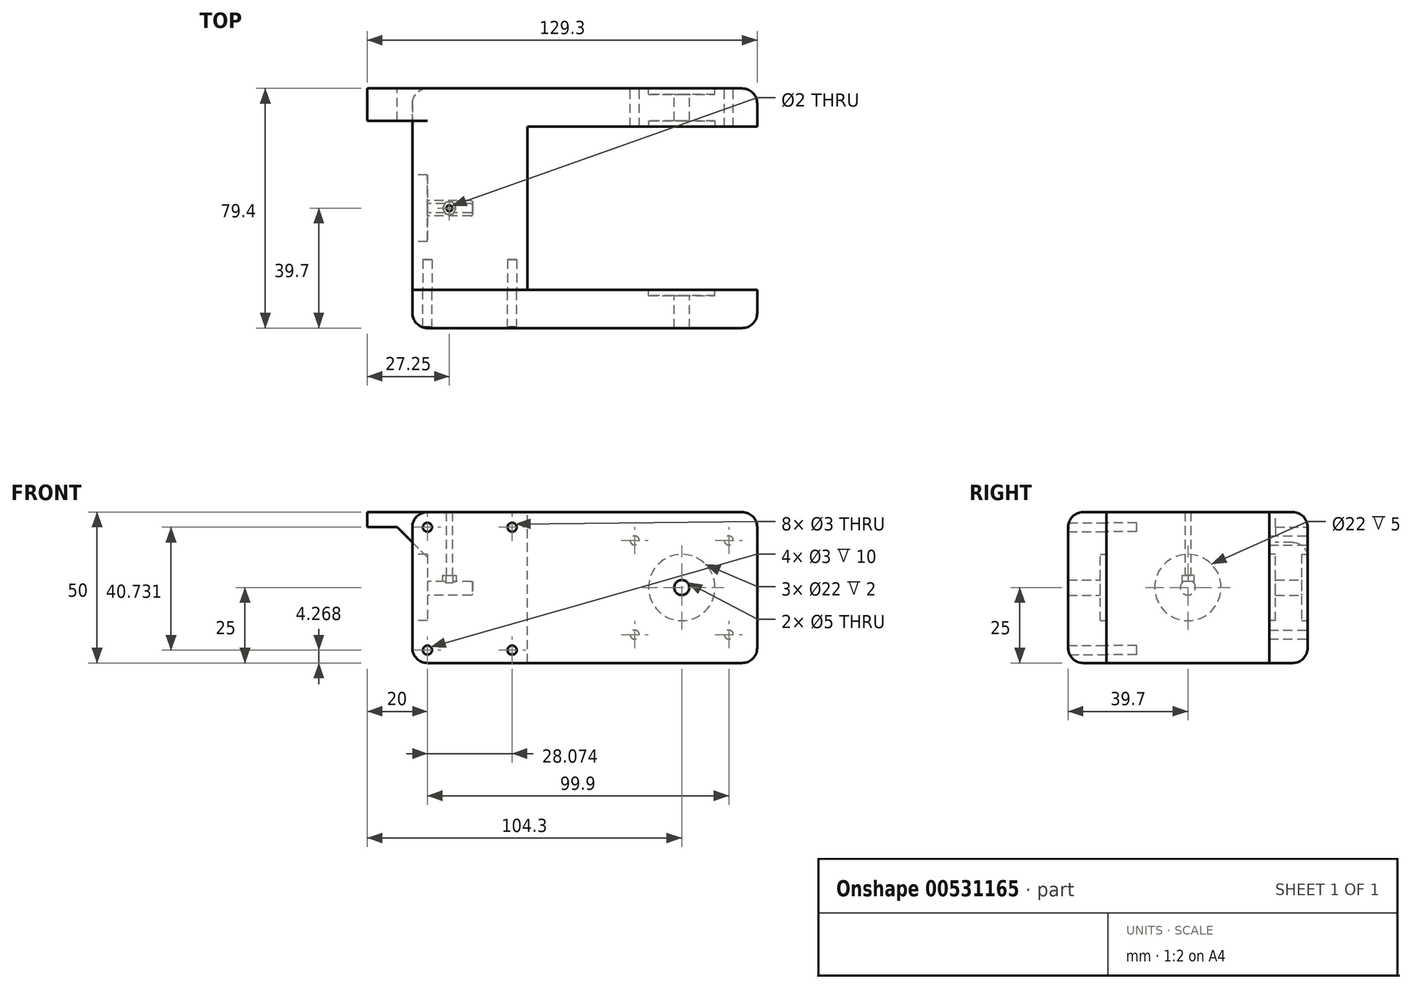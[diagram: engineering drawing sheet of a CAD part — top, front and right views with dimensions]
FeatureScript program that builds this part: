
annotation { "Feature Type Name" : "Feature", "Feature Type Description" : "" }
export const myFeature = defineFeature(function(context is Context, id is Id, definition is map)
    precondition{}
    {
        {
            var Q0;
            Q0=qCreatedBy(makeId("Front.planeOp"),FACE);
            var sketch = newSketch(context, id + "F0", { "sketchPlane" : qUnion([Q0])});
            skLineSegment(sketch, "E0.bottom", {"start": v(19.05, -25) * mm, "end": v(-19.05, -25) * mm});
            skLineSegment(sketch, "E0.top", {"start": v(19.05, 25) * mm, "end": v(-19.05, 25) * mm});
            skLineSegment(sketch, "E0.left", {"start": v(19.05, -25) * mm, "end": v(19.05, 25) * mm});
            skLineSegment(sketch, "E0.right", {"start": v(-19.05, -25) * mm, "end": v(-19.05, 25) * mm});
            skPoint(sketch, "E0.middle", {"position": v(0, 0) * mm});
            skSolve(sketch);
        }
        {
            var Q0;
            Q0 = qSketchRegion(id + "F0", true);
            extrude(context, id + "F1", {"entities" : qUnion([Q0]), "depth" : 54 * mm, "offsetDistance" : 25 * mm});
        }
        {
            var Q0;
            Q0=makeQuery(id+"F1.opExtrude","CAP_FACE",FACE,{"disambiguationData":[OSD([sQuery(id+"F0.wireOp",EDGE,"E0.bottom"),sQuery(id+"F0.wireOp",EDGE,"E0.top"),sQuery(id+"F0.wireOp",EDGE,"E0.left"),sQuery(id+"F0.wireOp",EDGE,"E0.right")])],"isStart":false});
            var sketch = newSketch(context, id + "F2", { "sketchPlane" : qUnion([Q0])});
            skLineSegment(sketch, "E1.bottom", {"start": v(-19.05, -25) * mm, "end": v(95.25, -25) * mm});
            skLineSegment(sketch, "E1.top", {"start": v(-19.05, 25) * mm, "end": v(95.25, 25) * mm});
            skLineSegment(sketch, "E1.left", {"start": v(-19.05, -25) * mm, "end": v(-19.05, 25) * mm});
            skLineSegment(sketch, "E1.right", {"start": v(95.25, -25) * mm, "end": v(95.25, 25) * mm});
            skSolve(sketch);
        }
        {
            var Q0;
            Q0 = qSketchRegion(id + "F2", true);
            extrude(context, id + "F3", {"entities" : qUnion([Q0]), "operationType" : NewBodyOperationType.ADD, "depth" : 12.7 * mm, "offsetDistance" : 25 * mm});
        }
        {
            var Q0;
            Q0=makeQuery(id+"F1.opExtrude","CAP_FACE",FACE,{"disambiguationData":[OSD([sQuery(id+"F0.wireOp",EDGE,"E0.bottom"),sQuery(id+"F0.wireOp",EDGE,"E0.top"),sQuery(id+"F0.wireOp",EDGE,"E0.left"),sQuery(id+"F0.wireOp",EDGE,"E0.right")])],"isStart":true});
            var sketch = newSketch(context, id + "F4", { "sketchPlane" : qUnion([Q0])});
            skLineSegment(sketch, "E2.bottom", {"start": v(19.05, -25) * mm, "end": v(-95.25, -25) * mm});
            skLineSegment(sketch, "E2.top", {"start": v(19.05, 25) * mm, "end": v(-95.25, 25) * mm});
            skLineSegment(sketch, "E2.left", {"start": v(19.05, -25) * mm, "end": v(19.05, 25) * mm});
            skLineSegment(sketch, "E2.right", {"start": v(-95.25, -25) * mm, "end": v(-95.25, 25) * mm});
            skSolve(sketch);
        }
        {
            var Q0;
            Q0 = qSketchRegion(id + "F4", true);
            extrude(context, id + "F5", {"entities" : qUnion([Q0]), "operationType" : NewBodyOperationType.ADD, "depth" : 12.7 * mm, "offsetDistance" : 25 * mm});
        }
        {
            var Q0;
            Q0 = qSketchRegion(id + "F2", true);
            extrude(context, id + "F6", {"entities" : qUnion([Q0]), "operationType" : NewBodyOperationType.ADD, "depth" : 12.7 * mm, "offsetDistance" : 25 * mm});
        }
        {
            var Q0;
            Q0=makeQuery(id+"F5.opExtrude","CAP_FACE",FACE,{"disambiguationData":[OSD([sQuery(id+"F4.wireOp",EDGE,"E2.bottom"),sQuery(id+"F4.wireOp",EDGE,"E2.top"),sQuery(id+"F4.wireOp",EDGE,"E2.left"),sQuery(id+"F4.wireOp",EDGE,"E2.right")])],"isStart":false});
            var sketch = newSketch(context, id + "F7", { "sketchPlane" : qUnion([Q0])});
            skPoint(sketch, "E3.middle", {"position": v(-70.25, 0) * mm});
            skLineSegment(sketch, "E4", {"start": v(-91.25, -16.76) * mm, "end": v(-87, -21) * mm});
            skLineSegment(sketch, "E5", {"start": v(-91.25, -16.76) * mm, "end": v(-91.25, 16.76) * mm});
            skLineSegment(sketch, "E6", {"start": v(-91.25, 16.76) * mm, "end": v(-87, 21) * mm});
            skLineSegment(sketch, "E7", {"start": v(-87, -21) * mm, "end": v(-53.5, -21) * mm});
            skLineSegment(sketch, "E8", {"start": v(-53.5, -21) * mm, "end": v(-49.25, -16.76) * mm});
            skLineSegment(sketch, "E9", {"start": v(-49.25, -16.76) * mm, "end": v(-49.25, 16.76) * mm});
            skLineSegment(sketch, "E10", {"start": v(-49.25, 16.76) * mm, "end": v(-53.5, 21) * mm});
            skLineSegment(sketch, "E11", {"start": v(-53.5, 21) * mm, "end": v(-87, 21) * mm});
            skLineSegment(sketch, "E12", {"start": v(-70.25, 0) * mm, "end": v(-49.25, 0) * mm, "construction": true});
            skLineSegment(sketch, "E13", {"start": v(-70.25, 0) * mm, "end": v(-70.25, 21) * mm, "construction": true});
            skLineSegment(sketch, "E14", {"start": v(-70.25, 0) * mm, "end": v(-70.25, -21) * mm, "construction": true});
            skLineSegment(sketch, "E15", {"start": v(-70.25, 0) * mm, "end": v(-91.25, 0) * mm, "construction": true});
            skLineSegment(sketch, "E16.bottom", {"start": v(-54.65, -15.6) * mm, "end": v(-85.85, -15.6) * mm});
            skLineSegment(sketch, "E16.top", {"start": v(-54.65, 15.6) * mm, "end": v(-85.85, 15.6) * mm});
            skLineSegment(sketch, "E16.left", {"start": v(-54.65, -15.6) * mm, "end": v(-54.65, 15.6) * mm});
            skLineSegment(sketch, "E16.right", {"start": v(-85.85, -15.6) * mm, "end": v(-85.85, 15.6) * mm});
            skCircle(sketch, "E17", {"center": v(-85.85, 15.6) * mm, "radius": 1.5 * mm});
            skCircle(sketch, "E18", {"center": v(-54.65, 15.6) * mm, "radius": 1.5 * mm});
            skCircle(sketch, "E19", {"center": v(-54.65, -15.6) * mm, "radius": 1.5 * mm});
            skCircle(sketch, "E20", {"center": v(-85.85, -15.6) * mm, "radius": 1.5 * mm});
            skLineSegment(sketch, "E21.bottom", {"start": v(-78.35, 21) * mm, "end": v(-62.15, 21) * mm});
            skLineSegment(sketch, "E21.top", {"start": v(-78.35, 33) * mm, "end": v(-62.15, 33) * mm});
            skLineSegment(sketch, "E21.left", {"start": v(-78.35, 21) * mm, "end": v(-78.35, 33) * mm});
            skLineSegment(sketch, "E21.right", {"start": v(-62.15, 21) * mm, "end": v(-62.15, 33) * mm});
            skLineSegment(sketch, "E22", {"start": v(-62.15, 21) * mm, "end": v(-53.5, 21) * mm, "construction": true});
            skLineSegment(sketch, "E23", {"start": v(-78.35, 21) * mm, "end": v(-87, 21) * mm, "construction": true});
            skLineSegment(sketch, "E24", {"start": v(-53.5, 21) * mm, "end": v(-53.5, 25) * mm, "construction": true});
            skLineSegment(sketch, "E25", {"start": v(-53.5, -21) * mm, "end": v(-53.5, -25) * mm, "construction": true});
            skLineSegment(sketch, "E26", {"start": v(-91.25, 16.76) * mm, "end": v(-95.25, 16.76) * mm, "construction": true});
            skSolve(sketch);
        }
        {
            var Q0;
            {var subQ0=sQuery(id+"F7.wireOp",EDGE,"E16.left");var subQ1=sQuery(id+"F7.wireOp",EDGE,"E16.top");var subQ2=makeQuery(id+"F7.imprint","INTERSECT",VERTEX,{"derivedFrom":[subQ1,subQ0]});Q0=makeQuery(id+"F7.imprint","IMPRINT",FACE,{"disambiguationData":[TD([[makeQuery(id+"F7.imprint","IMPRINT",EDGE,{"disambiguationData":[TD([[subQ2,-1.0]])],"derivedFrom":subQ1}),-1.0]])]});}
            var Q1;
            {var subQ0=sQuery(id+"F7.wireOp",EDGE,"E16.left");var subQ1=sQuery(id+"F7.wireOp",EDGE,"E16.top");var subQ2=makeQuery(id+"F7.imprint","INTERSECT",VERTEX,{"derivedFrom":[subQ1,subQ0]});Q1=makeQuery(id+"F7.imprint","IMPRINT",FACE,{"disambiguationData":[TD([[makeQuery(id+"F7.imprint","IMPRINT",EDGE,{"disambiguationData":[TD([[subQ2,-1.0]])],"derivedFrom":subQ1}),1.0]])]});}
            var Q2;
            {var subQ0=sQuery(id+"F7.wireOp",EDGE,"E16.right");var subQ1=sQuery(id+"F7.wireOp",EDGE,"E16.top");var subQ2=makeQuery(id+"F7.imprint","INTERSECT",VERTEX,{"derivedFrom":[subQ1,subQ0]});Q2=makeQuery(id+"F7.imprint","IMPRINT",FACE,{"disambiguationData":[TD([[makeQuery(id+"F7.imprint","IMPRINT",EDGE,{"disambiguationData":[TD([[subQ2,1.0]])],"derivedFrom":subQ1}),-1.0]])]});}
            var Q3;
            {var subQ0=sQuery(id+"F7.wireOp",EDGE,"E16.right");var subQ1=sQuery(id+"F7.wireOp",EDGE,"E16.top");var subQ2=makeQuery(id+"F7.imprint","INTERSECT",VERTEX,{"derivedFrom":[subQ1,subQ0]});Q3=makeQuery(id+"F7.imprint","IMPRINT",FACE,{"disambiguationData":[TD([[makeQuery(id+"F7.imprint","IMPRINT",EDGE,{"disambiguationData":[TD([[subQ2,1.0]])],"derivedFrom":subQ1}),1.0]])]});}
            var Q4;
            {var subQ0=sQuery(id+"F7.wireOp",EDGE,"E16.right");var subQ1=sQuery(id+"F7.wireOp",EDGE,"E16.bottom");var subQ2=makeQuery(id+"F7.imprint","INTERSECT",VERTEX,{"derivedFrom":[subQ1,subQ0]});Q4=makeQuery(id+"F7.imprint","IMPRINT",FACE,{"disambiguationData":[TD([[makeQuery(id+"F7.imprint","IMPRINT",EDGE,{"disambiguationData":[TD([[subQ2,1.0]])],"derivedFrom":subQ1}),-1.0]])]});}
            var Q5;
            {var subQ0=sQuery(id+"F7.wireOp",EDGE,"E16.right");var subQ1=sQuery(id+"F7.wireOp",EDGE,"E16.bottom");var subQ2=makeQuery(id+"F7.imprint","INTERSECT",VERTEX,{"derivedFrom":[subQ1,subQ0]});Q5=makeQuery(id+"F7.imprint","IMPRINT",FACE,{"disambiguationData":[TD([[makeQuery(id+"F7.imprint","IMPRINT",EDGE,{"disambiguationData":[TD([[subQ2,1.0]])],"derivedFrom":subQ1}),1.0]])]});}
            var Q6;
            {var subQ0=sQuery(id+"F7.wireOp",EDGE,"E16.left");var subQ1=sQuery(id+"F7.wireOp",EDGE,"E16.bottom");var subQ2=makeQuery(id+"F7.imprint","INTERSECT",VERTEX,{"derivedFrom":[subQ1,subQ0]});Q6=makeQuery(id+"F7.imprint","IMPRINT",FACE,{"disambiguationData":[TD([[makeQuery(id+"F7.imprint","IMPRINT",EDGE,{"disambiguationData":[TD([[subQ2,-1.0]])],"derivedFrom":subQ1}),-1.0]])]});}
            var Q7;
            {var subQ0=sQuery(id+"F7.wireOp",EDGE,"E16.left");var subQ1=sQuery(id+"F7.wireOp",EDGE,"E16.bottom");var subQ2=makeQuery(id+"F7.imprint","INTERSECT",VERTEX,{"derivedFrom":[subQ1,subQ0]});Q7=makeQuery(id+"F7.imprint","IMPRINT",FACE,{"disambiguationData":[TD([[makeQuery(id+"F7.imprint","IMPRINT",EDGE,{"disambiguationData":[TD([[subQ2,-1.0]])],"derivedFrom":subQ1}),1.0]])]});}
            extrude(context, id + "F8", {"entities" : qUnion([Q0, Q1, Q2, Q3, Q4, Q5, Q6, Q7]), "operationType" : NewBodyOperationType.REMOVE, "oppositeDirection" : true, "depth" : 25 * mm, "offsetDistance" : 25 * mm});
        }
        {
            var Q0;
            Q0=makeQuery(id+"F5.opExtrude","CAP_FACE",FACE,{"disambiguationData":[OSD([sQuery(id+"F4.wireOp",EDGE,"E2.bottom"),sQuery(id+"F4.wireOp",EDGE,"E2.top"),sQuery(id+"F4.wireOp",EDGE,"E2.left"),sQuery(id+"F4.wireOp",EDGE,"E2.right")])],"isStart":false});
            var sketch = newSketch(context, id + "F9", { "sketchPlane" : qUnion([Q0])});
            skCircle(sketch, "E27", {"center": v(-70.25, 0) * mm, "radius": 11 * mm});
            skLineSegment(sketch, "E28", {"start": v(-70.3, 25) * mm, "end": v(-70.3, 11) * mm, "construction": true});
            skLineSegment(sketch, "E29", {"start": v(-70.3, -11) * mm, "end": v(-70.3, -25) * mm, "construction": true});
            skSolve(sketch);
        }
        {
            var Q0;
            Q0 = qSketchRegion(id + "F9", true);
            extrude(context, id + "F10", {"entities" : qUnion([Q0]), "operationType" : NewBodyOperationType.REMOVE, "oppositeDirection" : true, "depth" : 2 * mm, "offsetDistance" : 25 * mm});
        }
        {
            var Q0;
            Q0=makeQuery(id+"F10.boolean.opBoolean","COPY",FACE,{"derivedFrom":makeQuery(id+"F10.opExtrude","CAP_FACE",FACE,{"disambiguationData":[OSD([sQuery(id+"F9.wireOp",EDGE,"E27")])],"isStart":false})});
            var sketch = newSketch(context, id + "F11", { "sketchPlane" : qUnion([Q0])});
            skCircle(sketch, "E30", {"center": v(-70.25, 0) * mm, "radius": 2.5 * mm});
            skSolve(sketch);
        }
        {
            var Q0;
            Q0 = qSketchRegion(id + "F11", true);
            extrude(context, id + "F12", {"entities" : qUnion([Q0]), "operationType" : NewBodyOperationType.REMOVE, "oppositeDirection" : true, "depth" : 106 * mm, "offsetDistance" : 25 * mm});
        }
        {
            var Q0;
            Q0=makeQuery(id+"F3.opExtrude","CAP_EDGE",EDGE,{"disambiguationData":[OSD([sQuery(id+"F2.wireOp",EDGE,"E1.top")])],"isStart":false});
            var Q1;
            Q1=makeQuery(id+"F3.opExtrude","SWEPT_EDGE",EDGE,{"disambiguationData":[OSD([sQuery(id+"F2.wireOp",EDGE,"E1.top"),sQuery(id+"F2.wireOp",EDGE,"E1.right")])]});
            var Q2;
            Q2=makeQuery(id+"F3.opExtrude","SWEPT_EDGE",EDGE,{"disambiguationData":[OSD([sQuery(id+"F2.wireOp",EDGE,"E1.bottom"),sQuery(id+"F2.wireOp",EDGE,"E1.right")])]});
            var Q3;
            Q3=makeQuery(id+"F3.opExtrude","CAP_EDGE",EDGE,{"disambiguationData":[OSD([sQuery(id+"F2.wireOp",EDGE,"E1.bottom")])],"isStart":false});
            var Q4;
            Q4=makeQuery(id+"F5.opExtrude","SWEPT_EDGE",EDGE,{"disambiguationData":[OSD([sQuery(id+"F4.wireOp",EDGE,"E2.top"),sQuery(id+"F4.wireOp",EDGE,"E2.right")])]});
            var Q5;
            Q5=makeQuery(id+"F5.opExtrude","SWEPT_EDGE",EDGE,{"disambiguationData":[OSD([sQuery(id+"F4.wireOp",EDGE,"E2.bottom"),sQuery(id+"F4.wireOp",EDGE,"E2.right")])]});
            var Q6;
            Q6=makeQuery(id+"F5.opExtrude","CAP_EDGE",EDGE,{"disambiguationData":[OSD([sQuery(id+"F4.wireOp",EDGE,"E2.top")])],"isStart":false});
            var Q7;
            Q7=makeQuery(id+"F5.opExtrude","CAP_EDGE",EDGE,{"disambiguationData":[OSD([sQuery(id+"F4.wireOp",EDGE,"E2.bottom")])],"isStart":false});
            var Q8;
            Q8=makeQuery(id+"F5.boolean.opBoolean","MERGE",EDGE,{"derivedFrom":[makeQuery(id+"F3.boolean.opBoolean","MERGE",EDGE,{"derivedFrom":[makeQuery(id+"F1.opExtrude","SWEPT_EDGE",EDGE,{"disambiguationData":[OSD([sQuery(id+"F0.wireOp",EDGE,"E0.top"),sQuery(id+"F0.wireOp",EDGE,"E0.right")])]}),makeQuery(id+"F3.opExtrude","SWEPT_EDGE",EDGE,{"disambiguationData":[OSD([sQuery(id+"F2.wireOp",EDGE,"E1.top"),sQuery(id+"F2.wireOp",EDGE,"E1.left")])]})]}),makeQuery(id+"F5.opExtrude","SWEPT_EDGE",EDGE,{"disambiguationData":[OSD([sQuery(id+"F4.wireOp",EDGE,"E2.top"),sQuery(id+"F4.wireOp",EDGE,"E2.left")])]})]});
            var Q9;
            Q9=makeQuery(id+"F5.boolean.opBoolean","MERGE",EDGE,{"derivedFrom":[makeQuery(id+"F3.boolean.opBoolean","MERGE",EDGE,{"derivedFrom":[makeQuery(id+"F1.opExtrude","SWEPT_EDGE",EDGE,{"disambiguationData":[OSD([sQuery(id+"F0.wireOp",EDGE,"E0.bottom"),sQuery(id+"F0.wireOp",EDGE,"E0.right")])]}),makeQuery(id+"F3.opExtrude","SWEPT_EDGE",EDGE,{"disambiguationData":[OSD([sQuery(id+"F2.wireOp",EDGE,"E1.bottom"),sQuery(id+"F2.wireOp",EDGE,"E1.left")])]})]}),makeQuery(id+"F5.opExtrude","SWEPT_EDGE",EDGE,{"disambiguationData":[OSD([sQuery(id+"F4.wireOp",EDGE,"E2.bottom"),sQuery(id+"F4.wireOp",EDGE,"E2.left")])]})]});
            var Q10;
            Q10=makeQuery(id+"F5.opExtrude","CAP_EDGE",EDGE,{"disambiguationData":[OSD([sQuery(id+"F4.wireOp",EDGE,"E2.right")])],"isStart":false});
            var Q11;
            Q11=makeQuery(id+"F3.opExtrude","CAP_EDGE",EDGE,{"disambiguationData":[OSD([sQuery(id+"F2.wireOp",EDGE,"E1.right")])],"isStart":false});
            var Q12;
            Q12=makeQuery(id+"F3.opExtrude","CAP_EDGE",EDGE,{"disambiguationData":[OSD([sQuery(id+"F2.wireOp",EDGE,"E1.left")])],"isStart":false});
            var Q13;
            Q13=makeQuery(id+"F5.opExtrude","CAP_EDGE",EDGE,{"disambiguationData":[OSD([sQuery(id+"F4.wireOp",EDGE,"E2.left")])],"isStart":false});
            fillet(context, id + "F13", {"entities" : qUnion([Q0, Q1, Q2, Q3, Q4, Q5, Q6, Q7, Q8, Q9, Q10, Q11, Q12, Q13]), "radius" : 5 * mm, "tangentPropagation" : true, "allowEdgeOverflow" : false});
        }
        {
            var Q0;
            Q0=makeQuery(id+"F3.opExtrude","CAP_FACE",FACE,{"disambiguationData":[OSD([sQuery(id+"F2.wireOp",EDGE,"E1.bottom"),sQuery(id+"F2.wireOp",EDGE,"E1.top"),sQuery(id+"F2.wireOp",EDGE,"E1.left"),sQuery(id+"F2.wireOp",EDGE,"E1.right")])],"isStart":true});
            var sketch = newSketch(context, id + "F14", { "sketchPlane" : qUnion([Q0])});
            skCircle(sketch, "E31", {"center": v(-70.25, 0) * mm, "radius": 11 * mm});
            skSolve(sketch);
        }
        {
            var Q0;
            Q0 = qSketchRegion(id + "F14", true);
            extrude(context, id + "F15", {"entities" : qUnion([Q0]), "operationType" : NewBodyOperationType.REMOVE, "oppositeDirection" : true, "depth" : 2 * mm, "offsetDistance" : 25 * mm});
        }
        {
            var Q0;
            Q0=makeQuery(id+"F5.opExtrude","CAP_FACE",FACE,{"disambiguationData":[OSD([sQuery(id+"F4.wireOp",EDGE,"E2.bottom"),sQuery(id+"F4.wireOp",EDGE,"E2.top"),sQuery(id+"F4.wireOp",EDGE,"E2.left"),sQuery(id+"F4.wireOp",EDGE,"E2.right")])],"isStart":true});
            var sketch = newSketch(context, id + "F16", { "sketchPlane" : qUnion([Q0])});
            skCircle(sketch, "E32", {"center": v(70.25, 0) * mm, "radius": 11 * mm});
            skSolve(sketch);
        }
        {
            var Q0;
            Q0 = qSketchRegion(id + "F16", true);
            extrude(context, id + "F17", {"entities" : qUnion([Q0]), "operationType" : NewBodyOperationType.REMOVE, "oppositeDirection" : true, "depth" : 2 * mm, "offsetDistance" : 25 * mm});
        }
        {
            var Q0;
            Q0=makeQuery(id+"F5.boolean.opBoolean","MERGE",FACE,{"derivedFrom":[makeQuery(id+"F3.boolean.opBoolean","MERGE",FACE,{"derivedFrom":[makeQuery(id+"F1.opExtrude","SWEPT_FACE",FACE,{"disambiguationData":[OSD([sQuery(id+"F0.wireOp",EDGE,"E0.top")])]}),makeQuery(id+"F3.opExtrude","SWEPT_FACE",FACE,{"disambiguationData":[OSD([sQuery(id+"F2.wireOp",EDGE,"E1.top")])]})]}),makeQuery(id+"F5.opExtrude","SWEPT_FACE",FACE,{"disambiguationData":[OSD([sQuery(id+"F4.wireOp",EDGE,"E2.top")])]})]});
            var sketch = newSketch(context, id + "F18", { "sketchPlane" : qUnion([Q0])});
            skLineSegment(sketch, "E33.bottom", {"start": v(-14.05, 12.7) * mm, "end": v(-34.05, 12.7) * mm});
            skLineSegment(sketch, "E33.top", {"start": v(-14.05, 2) * mm, "end": v(-34.05, 2) * mm});
            skLineSegment(sketch, "E33.left", {"start": v(-14.05, 12.7) * mm, "end": v(-14.05, 2) * mm});
            skLineSegment(sketch, "E33.right", {"start": v(-34.05, 12.7) * mm, "end": v(-34.05, 2) * mm});
            skSolve(sketch);
        }
        {
            var Q0;
            Q0 = qSketchRegion(id + "F18", true);
            extrude(context, id + "F19", {"entities" : qUnion([Q0]), "operationType" : NewBodyOperationType.ADD, "oppositeDirection" : true, "depth" : 5 * mm, "offsetDistance" : 25 * mm});
        }
        {
            var Q0;
            Q0=makeQuery(id+"F19.opExtrude","SWEPT_FACE",FACE,{"disambiguationData":[OSD([sQuery(id+"F18.wireOp",EDGE,"E33.bottom")])]});
            var sketch = newSketch(context, id + "F20", { "sketchPlane" : qUnion([Q0])});
            skLineSegment(sketch, "E34", {"start": v(14.05, 10) * mm, "end": v(24.05, 20) * mm});
            skLineSegment(sketch, "E35", {"start": v(24.05, 20) * mm, "end": v(14.05, 20) * mm});
            skLineSegment(sketch, "E36", {"start": v(14.05, 10) * mm, "end": v(14.05, 20) * mm});
            skSolve(sketch);
        }
        {
            var Q0;
            Q0 = qSketchRegion(id + "F20", true);
            var Q1;
            Q1=makeQuery(id+"F19.opExtrude","SWEPT_FACE",FACE,{"disambiguationData":[OSD([sQuery(id+"F18.wireOp",EDGE,"E33.top")])]});
            extrude(context, id + "F21", {"entities" : qUnion([Q0]), "operationType" : NewBodyOperationType.ADD, "endBound" : BoundingType.UP_TO_SURFACE, "oppositeDirection" : true, "depth" : 25 * mm, "endBoundEntityFace" : qUnion([Q1]), "offsetDistance" : 25 * mm});
        }
        {
            var Q0;
            Q0=makeQuery(id+"F19.opExtrude","CAP_EDGE",EDGE,{"disambiguationData":[OSD([sQuery(id+"F18.wireOp",EDGE,"E33.bottom")])],"isStart":true});
            fillet(context, id + "F22", {"entities" : qUnion([Q0]), "radius" : 5 * mm, "tangentPropagation" : true, "allowEdgeOverflow" : false});
        }
        {
            var Q0;
            Q0=makeQuery(id+"F19.boolean.opBoolean","MERGE",FACE,{"derivedFrom":[makeQuery(id+"F5.boolean.opBoolean","MERGE",FACE,{"derivedFrom":[makeQuery(id+"F3.boolean.opBoolean","MERGE",FACE,{"derivedFrom":[makeQuery(id+"F1.opExtrude","SWEPT_FACE",FACE,{"disambiguationData":[OSD([sQuery(id+"F0.wireOp",EDGE,"E0.top")])]}),makeQuery(id+"F3.opExtrude","SWEPT_FACE",FACE,{"disambiguationData":[OSD([sQuery(id+"F2.wireOp",EDGE,"E1.top")])]})]}),makeQuery(id+"F5.opExtrude","SWEPT_FACE",FACE,{"disambiguationData":[OSD([sQuery(id+"F4.wireOp",EDGE,"E2.top")])]})]}),makeQuery(id+"F19.opExtrude","CAP_FACE",FACE,{"disambiguationData":[OSD([sQuery(id+"F18.wireOp",EDGE,"E33.bottom"),sQuery(id+"F18.wireOp",EDGE,"E33.top"),sQuery(id+"F18.wireOp",EDGE,"E33.left"),sQuery(id+"F18.wireOp",EDGE,"E33.right")])],"isStart":true})]});
            var sketch = newSketch(context, id + "F23", { "sketchPlane" : qUnion([Q0])});
            skLineSegment(sketch, "E37.bottom", {"start": v(19.05, 0) * mm, "end": v(-14.05, 0) * mm});
            skLineSegment(sketch, "E37.top", {"start": v(19.05, -13) * mm, "end": v(-14.05, -13) * mm});
            skLineSegment(sketch, "E37.left", {"start": v(19.05, 0) * mm, "end": v(19.05, -13) * mm});
            skLineSegment(sketch, "E37.right", {"start": v(-14.05, 0) * mm, "end": v(-14.05, -13) * mm});
            skSolve(sketch);
        }
        {
            var Q0;
            Q0 = qSketchRegion(id + "F23", true);
            extrude(context, id + "F24", {"entities" : qUnion([Q0]), "operationType" : NewBodyOperationType.ADD, "depth" : 40 * mm, "offsetDistance" : 25 * mm});
        }
        {
            var Q0;
            Q0=makeQuery(id+"F24.opExtrude","CAP_EDGE",EDGE,{"disambiguationData":[OSD([sQuery(id+"F23.wireOp",EDGE,"E37.left")])],"isStart":false});
            chamfer(context, id + "F25", {"entities" : qUnion([Q0]), "width" : 20 * mm, "tangentPropagation" : true});
        }
        {
            var Q0;
            Q0=makeQuery(id+"F24.opExtrude","SWEPT_FACE",FACE,{"disambiguationData":[OSD([sQuery(id+"F23.wireOp",EDGE,"E37.top")])]});
            var sketch = newSketch(context, id + "F26", { "sketchPlane" : qUnion([Q0])});
            skCircle(sketch, "E38", {"center": v(12, 45.26) * mm, "radius": 1.6 * mm});
            skCircle(sketch, "E39", {"center": v(-9.96, 57.8) * mm, "radius": 1.6 * mm});
            skLineSegment(sketch, "E40.left", {"start": v(14.04, 46.7) * mm, "end": v(0.93, 65.42) * mm});
            skLineSegment(sketch, "E40.right", {"start": v(1.1, 37.63) * mm, "end": v(-12, 56.36) * mm});
            skLineSegment(sketch, "E41", {"start": v(13.42, 43.2) * mm, "end": v(4.59, 37.02) * mm});
            skLineSegment(sketch, "E42", {"start": v(-2.56, 66.03) * mm, "end": v(-11.4, 59.84) * mm});
            skArc(sketch, "E43", {"start": v(13.42, 43.2) * mm, "mid": v(14.45, 44.82) * mm, "end": v(14.04, 46.7) * mm});
            skArc(sketch, "E44", {"start": v(1.1, 37.63) * mm, "mid": v(2.72, 36.6) * mm, "end": v(4.59, 37.02) * mm});
            skArc(sketch, "E45", {"start": v(0.93, 65.42) * mm, "mid": v(-0.69, 66.44) * mm, "end": v(-2.56, 66.03) * mm});
            skArc(sketch, "E46", {"start": v(-11.4, 59.84) * mm, "mid": v(-12.42, 58.23) * mm, "end": v(-12, 56.36) * mm});
            skSolve(sketch);
        }
        {
            var Q0;
            Q0=makeQuery(id+"F26.imprint","IMPRINT",FACE,{"disambiguationData":[TD([[makeQuery(id+"F26.imprint","IMPRINT",EDGE,{"derivedFrom":sQuery(id+"F26.wireOp",EDGE,"E39")}),1.0]])]});
            var Q1;
            Q1=makeQuery(id+"F26.imprint","IMPRINT",FACE,{"disambiguationData":[TD([[makeQuery(id+"F26.imprint","IMPRINT",EDGE,{"derivedFrom":sQuery(id+"F26.wireOp",EDGE,"E38")}),1.0]])]});
            extrude(context, id + "F27", {"entities" : qUnion([Q0, Q1]), "operationType" : NewBodyOperationType.REMOVE, "oppositeDirection" : true, "depth" : 1 * mm, "offsetDistance" : 25 * mm});
        }
        {
            var Q0;
            Q0=makeQuery(id+"F1.opExtrude","SWEPT_FACE",FACE,{"disambiguationData":[OSD([sQuery(id+"F0.wireOp",EDGE,"E0.right")])]});
            var sketch = newSketch(context, id + "F28", { "sketchPlane" : qUnion([Q0])});
            skCircle(sketch, "E47", {"center": v(27, 0) * mm, "radius": 11 * mm});
            skLineSegment(sketch, "E48", {"start": v(38, 0) * mm, "end": v(61.7, 0) * mm, "construction": true});
            skLineSegment(sketch, "E49", {"start": v(16, 0) * mm, "end": v(-7.7, 0) * mm, "construction": true});
            skSolve(sketch);
        }
        {
            var Q0;
            Q0 = qSketchRegion(id + "F28", true);
            extrude(context, id + "F29", {"entities" : qUnion([Q0]), "operationType" : NewBodyOperationType.REMOVE, "oppositeDirection" : true, "depth" : 5 * mm, "offsetDistance" : 25 * mm});
        }
        {
            var Q0;
            Q0=makeQuery(id+"F29.boolean.opBoolean","COPY",FACE,{"derivedFrom":makeQuery(id+"F29.opExtrude","CAP_FACE",FACE,{"disambiguationData":[OSD([sQuery(id+"F28.wireOp",EDGE,"E47")])],"isStart":false})});
            var sketch = newSketch(context, id + "F30", { "sketchPlane" : qUnion([Q0])});
            skArc(sketch, "E50", {"start": v(25.5, 2) * mm, "mid": v(27, -2.5) * mm, "end": v(28.5, 2) * mm});
            skLineSegment(sketch, "E51", {"start": v(25.5, 2) * mm, "end": v(28.5, 2) * mm});
            skSolve(sketch);
        }
        {
            var Q0;
            Q0=makeQuery(id+"F30.imprint","IMPRINT",FACE,{"disambiguationData":[TD([[makeQuery(id+"F30.imprint","IMPRINT",EDGE,{"derivedFrom":sQuery(id+"F30.wireOp",EDGE,"E50")}),1.0]])]});
            extrude(context, id + "F31", {"entities" : qUnion([Q0]), "operationType" : NewBodyOperationType.REMOVE, "oppositeDirection" : true, "depth" : 15 * mm, "offsetDistance" : 25 * mm});
        }
        {
            var Q0;
            Q0=makeQuery(id+"F31.boolean.opBoolean","COPY",EDGE,{"derivedFrom":makeQuery(id+"F31.opExtrude","CAP_EDGE",EDGE,{"disambiguationData":[OSD([sQuery(id+"F30.wireOp",EDGE,"E50")])],"isStart":false})});
            fillet(context, id + "F32", {"entities" : qUnion([Q0]), "radius" : .5 * mm, "tangentPropagation" : true, "allowEdgeOverflow" : false});
        }
        {
            var Q0;
            Q0=makeQuery(id+"F31.boolean.opBoolean","COPY",FACE,{"derivedFrom":makeQuery(id+"F31.opExtrude","SWEPT_FACE",FACE,{"disambiguationData":[OSD([sQuery(id+"F30.wireOp",EDGE,"E51")])]})});
            var sketch = newSketch(context, id + "F33", { "sketchPlane" : qUnion([Q0])});
            skCircle(sketch, "E52", {"center": v(-6.8, 27) * mm, "radius": 1 * mm});
            skLineSegment(sketch, "E53", {"start": v(-14.05, 27) * mm, "end": v(0.45, 27) * mm, "construction": true});
            skCircle(sketch, "E54.cCircle", {"center": v(-6.8, 27) * mm, "radius": 2 * mm, "construction": true});
            skLineSegment(sketch, "E54.0", {"start": v(-5.65, 29) * mm, "end": v(-4.5, 27) * mm});
            skLineSegment(sketch, "E54.1", {"start": v(-4.5, 27) * mm, "end": v(-5.65, 25) * mm});
            skLineSegment(sketch, "E54.2", {"start": v(-5.65, 25) * mm, "end": v(-7.95, 25) * mm});
            skLineSegment(sketch, "E54.3", {"start": v(-7.95, 25) * mm, "end": v(-9.1, 27) * mm});
            skLineSegment(sketch, "E54.4", {"start": v(-9.1, 27) * mm, "end": v(-7.95, 29) * mm});
            skLineSegment(sketch, "E54.5", {"start": v(-7.95, 29) * mm, "end": v(-5.65, 29) * mm});
            skPoint(sketch, "E54.0.midPoint", {"position": v(-5.07, 28) * mm});
            skSolve(sketch);
        }
        {
            var Q0;
            Q0 = qSketchRegion(id + "F33", true);
            extrude(context, id + "F34", {"entities" : qUnion([Q0]), "operationType" : NewBodyOperationType.REMOVE, "oppositeDirection" : true, "depth" : 2 * mm, "offsetDistance" : 25 * mm, "hasSecondDirection" : true, "secondDirectionOppositeDirection" : false, "secondDirectionDepth" : 1 * mm});
        }
        {
            var Q0;
            Q0=makeQuery(id+"F34.boolean.opBoolean","SPLIT",FACE,{"disambiguationData":[TD([makeQuery(id+"F34.opExtrude","SWEPT_FACE",FACE,{"disambiguationData":[OSD([sQuery(id+"F33.wireOp",EDGE,"E52")])]})])],"derivedFrom":makeQuery(id+"F31.boolean.opBoolean","COPY",FACE,{"derivedFrom":makeQuery(id+"F31.opExtrude","SWEPT_FACE",FACE,{"disambiguationData":[OSD([sQuery(id+"F30.wireOp",EDGE,"E51")])]})})});
            extrude(context, id + "F35", {"entities" : qUnion([Q0]), "operationType" : NewBodyOperationType.REMOVE, "oppositeDirection" : true, "depth" : 25 * mm, "offsetDistance" : 25 * mm});
        }
        {
            var Q0;
            Q0=makeQuery(id+"F3.opExtrude","CAP_FACE",FACE,{"disambiguationData":[OSD([sQuery(id+"F2.wireOp",EDGE,"E1.bottom"),sQuery(id+"F2.wireOp",EDGE,"E1.top"),sQuery(id+"F2.wireOp",EDGE,"E1.left"),sQuery(id+"F2.wireOp",EDGE,"E1.right")])],"isStart":false});
            var sketch = newSketch(context, id + "F36", { "sketchPlane" : qUnion([Q0])});
            skLineSegment(sketch, "E55.bottom", {"start": v(-29.95, -38.06) * mm, "end": v(108.68, -38.06) * mm});
            skLineSegment(sketch, "E55.top", {"start": v(-29.95, 25.37) * mm, "end": v(108.68, 25.37) * mm});
            skLineSegment(sketch, "E55.left", {"start": v(-29.95, -38.06) * mm, "end": v(-29.95, 25.37) * mm});
            skLineSegment(sketch, "E55.right", {"start": v(108.68, -38.06) * mm, "end": v(108.68, 25.37) * mm});
            skSolve(sketch);
        }
        {
            var Q0;
            Q0 = qSketchRegion(id + "F36", true);
            var Q1;
            Q1=makeQuery(id+"F3.opExtrude","CAP_FACE",FACE,{"disambiguationData":[OSD([sQuery(id+"F2.wireOp",EDGE,"E1.bottom"),sQuery(id+"F2.wireOp",EDGE,"E1.top"),sQuery(id+"F2.wireOp",EDGE,"E1.left"),sQuery(id+"F2.wireOp",EDGE,"E1.right")])],"isStart":true});
            extrude(context, id + "F37", {"entities" : qUnion([Q0]), "operationType" : NewBodyOperationType.REMOVE, "endBound" : BoundingType.UP_TO_SURFACE, "oppositeDirection" : true, "depth" : 1 * mm, "endBoundEntityFace" : qUnion([Q1]), "offsetDistance" : 25 * mm});
        }
        {
            var Q0;
            Q0=makeQuery(id+"F37.boolean.opBoolean","COPY",FACE,{"derivedFrom":makeQuery(id+"F37.opExtrude","CAP_FACE",FACE,{"disambiguationData":[OSD([sQuery(id+"F36.wireOp",EDGE,"E55.bottom"),sQuery(id+"F36.wireOp",EDGE,"E55.top"),sQuery(id+"F36.wireOp",EDGE,"E55.left"),sQuery(id+"F36.wireOp",EDGE,"E55.right")])],"isStart":false})});
            var sketch = newSketch(context, id + "F38", { "sketchPlane" : qUnion([Q0])});
            skLineSegment(sketch, "E56.bottom", {"start": v(-19.05, -25) * mm, "end": v(95.25, -25) * mm});
            skLineSegment(sketch, "E56.top", {"start": v(-19.05, 25) * mm, "end": v(95.25, 25) * mm});
            skLineSegment(sketch, "E56.left", {"start": v(-19.05, -25) * mm, "end": v(-19.05, 25) * mm});
            skLineSegment(sketch, "E56.right", {"start": v(95.25, -25) * mm, "end": v(95.25, 25) * mm});
            skCircle(sketch, "E57", {"center": v(70.25, 0) * mm, "radius": 11 * mm});
            skCircle(sketch, "E58", {"center": v(70.25, 0) * mm, "radius": 2.5 * mm});
            skLineSegment(sketch, "E59.bottom", {"start": v(-14.05, 20) * mm, "end": v(14.02, 20) * mm, "construction": true});
            skLineSegment(sketch, "E59.top", {"start": v(-14.05, -20.73) * mm, "end": v(14.02, -20.73) * mm, "construction": true});
            skLineSegment(sketch, "E59.left", {"start": v(-14.05, 20) * mm, "end": v(-14.05, -20.73) * mm, "construction": true});
            skLineSegment(sketch, "E59.right", {"start": v(14.02, 20) * mm, "end": v(14.02, -20.73) * mm, "construction": true});
            skCircle(sketch, "E60", {"center": v(-14.05, 20) * mm, "radius": 1.5 * mm});
            skCircle(sketch, "E61", {"center": v(14.02, 20) * mm, "radius": 1.5 * mm});
            skCircle(sketch, "E62", {"center": v(-14.05, -20.73) * mm, "radius": 1.5 * mm});
            skCircle(sketch, "E63", {"center": v(14.02, -20.73) * mm, "radius": 1.5 * mm});
            skSolve(sketch);
        }
        {
            var Q0;
            Q0=makeQuery(id+"F38.imprint","IMPRINT",FACE,{"disambiguationData":[TD([[makeQuery(id+"F38.imprint","IMPRINT",EDGE,{"derivedFrom":sQuery(id+"F38.wireOp",EDGE,"E57")}),1.0]])]});
            var Q1;
            {var subQ0=sQuery(id+"F38.wireOp",EDGE,"E56.right");Q1=makeQuery(id+"F38.imprint","IMPRINT",FACE,{"disambiguationData":[TD([[makeQuery(id+"F38.imprint","IMPRINT",EDGE,{"derivedFrom":subQ0}),1.0]])]});}
            var Q2;
            Q2=makeQuery(id+"F38.imprint","IMPRINT",FACE,{"disambiguationData":[TD([[makeQuery(id+"F38.imprint","IMPRINT",EDGE,{"derivedFrom":sQuery(id+"F38.wireOp",EDGE,"E60")}),-1.0]])]});
            extrude(context, id + "F39", {"entities" : qUnion([Q0, Q1, Q2]), "depth" : 12.7 * mm, "offsetDistance" : 25 * mm});
        }
        {
            var Q0;
            Q0=makeQuery(id+"F39.opExtrude","SWEPT_EDGE",EDGE,{"disambiguationData":[OSD([sQuery(id+"F38.wireOp",EDGE,"E56.top"),sQuery(id+"F38.wireOp",EDGE,"E56.right")])]});
            var Q1;
            Q1=makeQuery(id+"F39.opExtrude","SWEPT_EDGE",EDGE,{"disambiguationData":[OSD([sQuery(id+"F38.wireOp",EDGE,"E56.bottom"),sQuery(id+"F38.wireOp",EDGE,"E56.right")])]});
            var Q2;
            Q2=makeQuery(id+"F39.opExtrude","CAP_EDGE",EDGE,{"disambiguationData":[OSD([sQuery(id+"F38.wireOp",EDGE,"E56.right")])],"isStart":false});
            var Q3;
            Q3=makeQuery(id+"F39.opExtrude","CAP_EDGE",EDGE,{"disambiguationData":[OSD([sQuery(id+"F38.wireOp",EDGE,"E56.top")])],"isStart":false});
            fillet(context, id + "F40", {"entities" : qUnion([Q0, Q1, Q2, Q3]), "radius" : 5 * mm, "tangentPropagation" : true, "allowEdgeOverflow" : false});
        }
        {
            var Q0;
            Q0=makeQuery(id+"F38.imprint","IMPRINT",FACE,{"disambiguationData":[TD([[makeQuery(id+"F38.imprint","IMPRINT",EDGE,{"derivedFrom":sQuery(id+"F38.wireOp",EDGE,"E57")}),1.0]])]});
            extrude(context, id + "F41", {"entities" : qUnion([Q0]), "operationType" : NewBodyOperationType.REMOVE, "depth" : 2 * mm, "offsetDistance" : 25 * mm});
        }
        {
            var Q0;
            Q0=makeQuery(id+"F38.imprint","IMPRINT",FACE,{"disambiguationData":[TD([[makeQuery(id+"F38.imprint","IMPRINT",EDGE,{"derivedFrom":sQuery(id+"F38.wireOp",EDGE,"E60")}),1.0]])]});
            var Q1;
            Q1=makeQuery(id+"F38.imprint","IMPRINT",FACE,{"disambiguationData":[TD([[makeQuery(id+"F38.imprint","IMPRINT",EDGE,{"derivedFrom":sQuery(id+"F38.wireOp",EDGE,"E61")}),1.0]])]});
            var Q2;
            Q2=makeQuery(id+"F38.imprint","IMPRINT",FACE,{"disambiguationData":[TD([[makeQuery(id+"F38.imprint","IMPRINT",EDGE,{"derivedFrom":sQuery(id+"F38.wireOp",EDGE,"E63")}),1.0]])]});
            var Q3;
            Q3=makeQuery(id+"F38.imprint","IMPRINT",FACE,{"disambiguationData":[TD([[makeQuery(id+"F38.imprint","IMPRINT",EDGE,{"derivedFrom":sQuery(id+"F38.wireOp",EDGE,"E62")}),1.0]])]});
            extrude(context, id + "F42", {"entities" : qUnion([Q0, Q1, Q2, Q3]), "operationType" : NewBodyOperationType.REMOVE, "oppositeDirection" : true, "depth" : 10 * mm, "offsetDistance" : 25 * mm});
        }
        {
            var Q0;
            Q0=makeQuery(id+"F24.opExtrude","CAP_FACE",FACE,{"disambiguationData":[OSD([sQuery(id+"F23.wireOp",EDGE,"E37.bottom"),sQuery(id+"F23.wireOp",EDGE,"E37.top"),sQuery(id+"F23.wireOp",EDGE,"E37.left"),sQuery(id+"F23.wireOp",EDGE,"E37.right")])],"isStart":false});
            var sketch = newSketch(context, id + "F43", { "sketchPlane" : qUnion([Q0])});
            skLineSegment(sketch, "E64.bottom", {"start": v(-49.75, 21.35) * mm, "end": v(35.65, 21.35) * mm});
            skLineSegment(sketch, "E64.top", {"start": v(-49.75, -15.78) * mm, "end": v(35.65, -15.78) * mm});
            skLineSegment(sketch, "E64.left", {"start": v(-49.75, 21.35) * mm, "end": v(-49.75, -15.78) * mm});
            skLineSegment(sketch, "E64.right", {"start": v(35.65, 21.35) * mm, "end": v(35.65, -15.78) * mm});
            skSolve(sketch);
        }
        {
            var Q0;
            Q0 = qSketchRegion(id + "F43", true);
            var Q1;
            {var subQ1=sQuery(id+"F2.wireOp",EDGE,"E1.top");var subQ3=sQuery(id+"F4.wireOp",EDGE,"E2.top");var subQ4=sQuery(id+"F0.wireOp",EDGE,"E0.top");Q1=makeQuery(id+"F24.boolean.opBoolean","SPLIT",FACE,{"disambiguationData":[TD([makeQuery(id+"F13.opFillet","BLEND_FACE",FACE,{"disambiguationData":[OSD([subQ1])]})])],"derivedFrom":makeQuery(id+"F19.boolean.opBoolean","MERGE",FACE,{"derivedFrom":[makeQuery(id+"F5.boolean.opBoolean","MERGE",FACE,{"derivedFrom":[makeQuery(id+"F3.boolean.opBoolean","MERGE",FACE,{"derivedFrom":[makeQuery(id+"F1.opExtrude","SWEPT_FACE",FACE,{"disambiguationData":[OSD([subQ4])]}),makeQuery(id+"F3.opExtrude","SWEPT_FACE",FACE,{"disambiguationData":[OSD([subQ1])]})]}),makeQuery(id+"F5.opExtrude","SWEPT_FACE",FACE,{"disambiguationData":[OSD([subQ3])]})]}),makeQuery(id+"F19.opExtrude","CAP_FACE",FACE,{"disambiguationData":[OSD([sQuery(id+"F18.wireOp",EDGE,"E33.bottom"),sQuery(id+"F18.wireOp",EDGE,"E33.top"),sQuery(id+"F18.wireOp",EDGE,"E33.left"),sQuery(id+"F18.wireOp",EDGE,"E33.right")])],"isStart":true})]})});}
            extrude(context, id + "F44", {"entities" : qUnion([Q0]), "operationType" : NewBodyOperationType.REMOVE, "endBound" : BoundingType.UP_TO_SURFACE, "oppositeDirection" : true, "depth" : 25 * mm, "endBoundEntityFace" : qUnion([Q1]), "offsetDistance" : 25 * mm});
        }
    });
